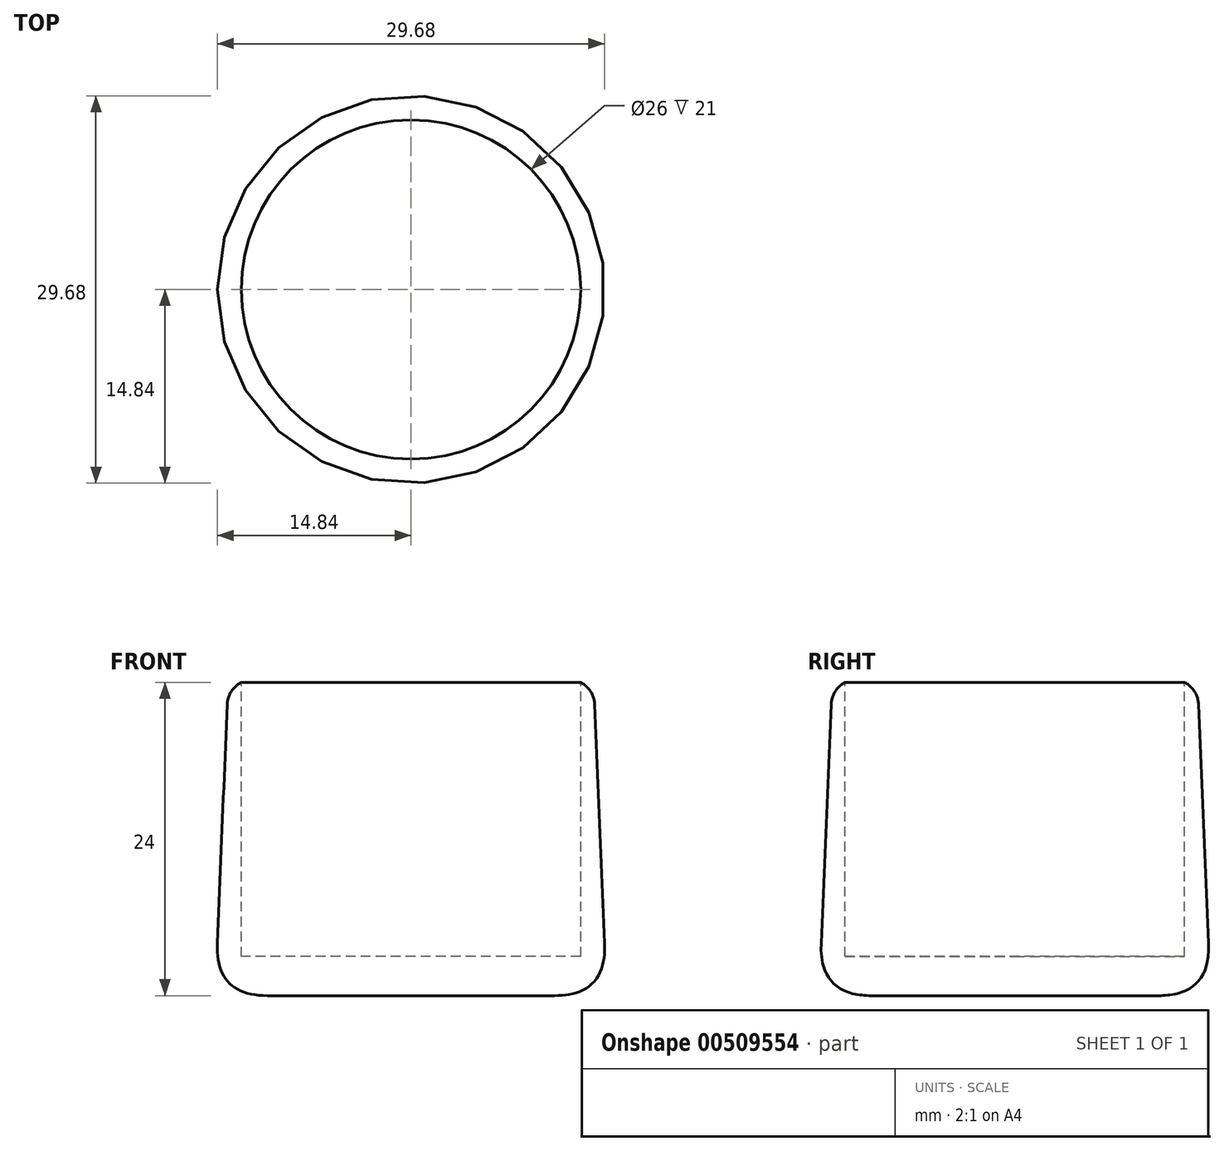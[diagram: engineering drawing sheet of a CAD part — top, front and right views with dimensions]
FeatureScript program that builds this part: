
annotation { "Feature Type Name" : "Feature", "Feature Type Description" : "" }
export const myFeature = defineFeature(function(context is Context, id is Id, definition is map)
    precondition{}
    {
        {
            var Q0;
            Q0=qCreatedBy(makeId("Front.planeOp"),FACE);
            var sketch = newSketch(context, id + "F0", { "sketchPlane" : qUnion([Q0])});
            skLineSegment(sketch, "E0", {"start": v(0, 0) * mm, "end": v(15, 0) * mm});
            skLineSegment(sketch, "E1", {"start": v(0, 0) * mm, "end": v(0, 24) * mm});
            skLineSegment(sketch, "E2", {"start": v(0, 24) * mm, "end": v(14, 24) * mm});
            skLineSegment(sketch, "E3", {"start": v(14, 24) * mm, "end": v(15, 0) * mm});
            skSolve(sketch);
        }
        {
            var Q0;
            Q0 = qSketchRegion(id + "F0", true);
            var Q1;
            Q1 = qSketchRegion(id + "F2", true);
            var Q2;
            Q2=sQuery(id+"F0.wireOp",EDGE,"E1");
            revolve(context, id + "F1", {"surfaceOperationType" : NewSurfaceOperationType.NEW, "entities" : qUnion([Q0, Q1]), "axis" : qUnion([Q2]), "revolveType" : RevolveType.FULL});
        }
        {
            var Q0;
            Q0=makeQuery(id+"F1.opRevolve","SWEPT_FACE",FACE,{"disambiguationData":[OSD([sQuery(id+"F0.wireOp",EDGE,"E2")])]});
            var sketch = newSketch(context, id + "F2", { "sketchPlane" : qUnion([Q0])});
            skCircle(sketch, "E4", {"center": v(0, 0) * mm, "radius": 13 * mm});
            skSolve(sketch);
        }
        {
            var Q0;
            Q0=makeQuery(id+"F2.imprint","IMPRINT",FACE,{"disambiguationData":[TD([[makeQuery(id+"F2.imprint","IMPRINT",EDGE,{"derivedFrom":sQuery(id+"F2.wireOp",EDGE,"E4")}),1.0]])]});
            extrude(context, id + "F3", {"entities" : qUnion([Q0]), "operationType" : NewBodyOperationType.REMOVE, "flatOperationType" : FlatOperationType.REMOVE, "oppositeDirection" : true, "offsetDistance" : 25 * mm, "depth" : 21 * mm, "domain" : OperationDomain.MODEL});
        }
        {
            var Q0;
            Q0=makeQuery(id+"F1.opRevolve","SWEPT_FACE",FACE,{"disambiguationData":[OSD([sQuery(id+"F0.wireOp",EDGE,"E0")])]});
            fillet(context, id + "F4", {"entities" : qUnion([Q0]), "radius" : 3.85 * mm, "tangentPropagation" : true, "rho" : 0.5, "crossSection" : FilletCrossSection.CONIC, "allowEdgeOverflow" : false});
        }
        {
            var Q0;
            Q0=makeQuery(id+"F1.opRevolve","SWEPT_EDGE",EDGE,{"disambiguationData":[OSD([sQuery(id+"F0.wireOp",EDGE,"E2"),sQuery(id+"F0.wireOp",EDGE,"E3")])]});
            fillet(context, id + "F5", {"entities" : qUnion([Q0]), "radius" : 2 * mm, "tangentPropagation" : true, "defaultsChanged" : true, "vertexSettings" : [], "allowEdgeOverflow" : false});
        }
    });
